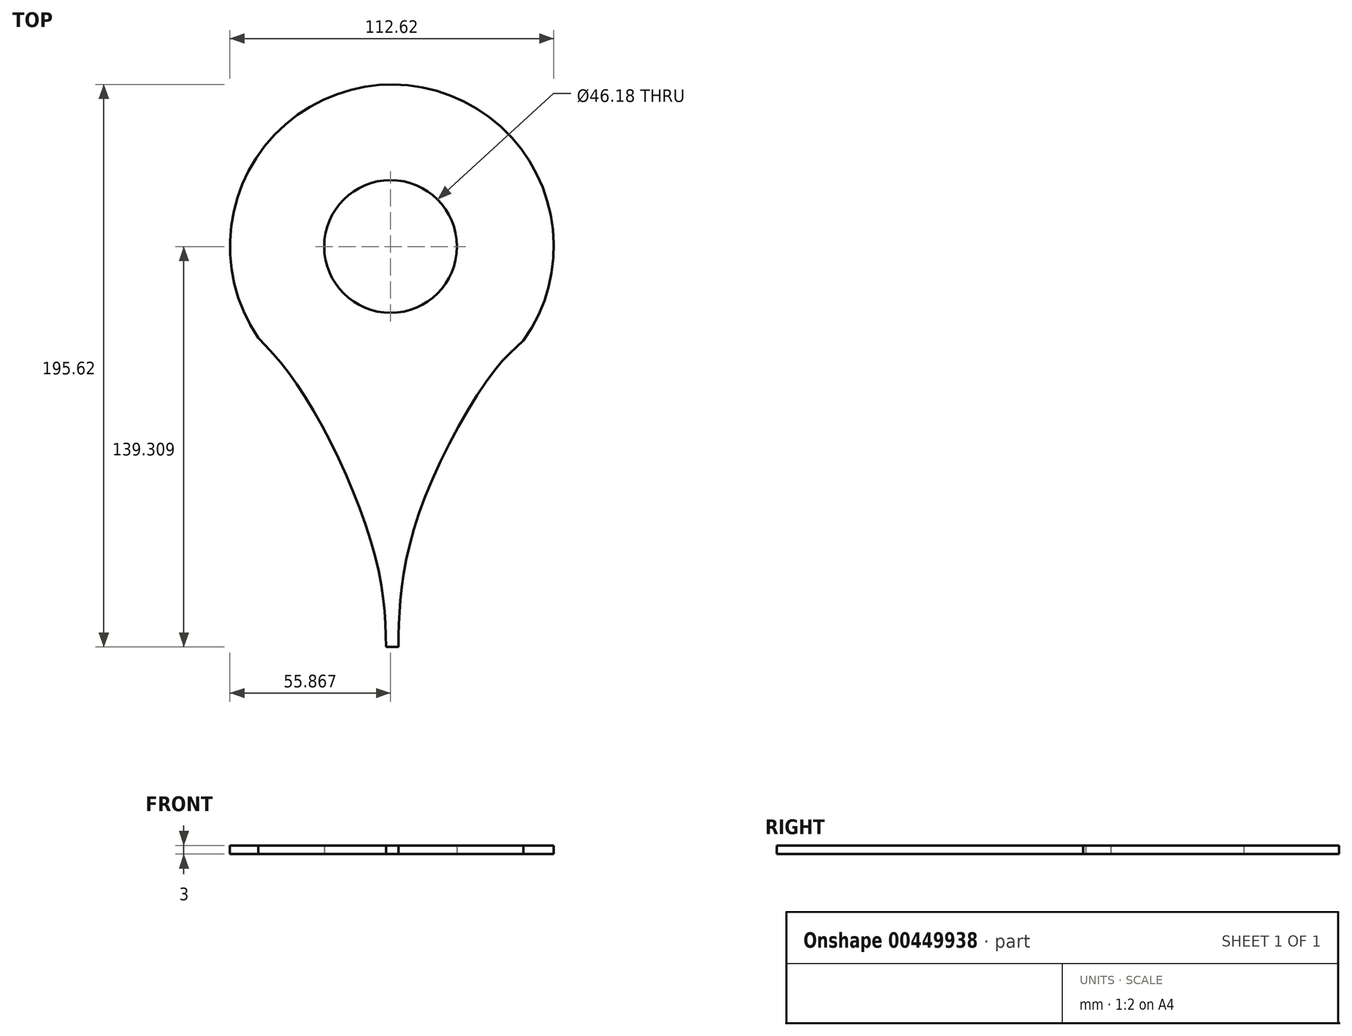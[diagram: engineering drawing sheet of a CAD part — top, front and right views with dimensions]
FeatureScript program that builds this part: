
annotation { "Feature Type Name" : "Feature", "Feature Type Description" : "" }
export const myFeature = defineFeature(function(context is Context, id is Id, definition is map)
    precondition{}
    {
        {
            var Q0;
            Q0=qCreatedBy(makeId("Top.planeOp"),FACE);
            var sketch = newSketch(context, id + "F0", { "sketchPlane" : qUnion([Q0])});
            skCircle(sketch, "E0", {"center": v(-15.91, 53.5) * mm, "radius": 23.09 * mm});
            skPoint(sketch, "E0.first.point", {"position": v(-33.82, 68.09) * mm});
            skPoint(sketch, "E0.second.point", {"position": v(6.07, 60.56) * mm});
            skPoint(sketch, "E0.third.point", {"position": v(-14.4, 30.47) * mm});
            skSolve(sketch);
        }
        {
            var Q0;
            Q0=qCreatedBy(makeId("Top.planeOp"),FACE);
            var sketch = newSketch(context, id + "F1", { "sketchPlane" : qUnion([Q0])});
            skArc(sketch, "E1", {"start": v(24.44, 13.77) * mm, "mid": v(-14.44, 109.8) * mm, "end": v(-56.8, 15.26) * mm});
            skPoint(sketch, "E1.first.point", {"position": v(-61.18, 86.39) * mm});
            skPoint(sketch, "E1.second.point", {"position": v(6.74, 105.25) * mm});
            skPoint(sketch, "E1.third.point", {"position": v(40.25, 61.65) * mm});
            skFitSpline(sketch, "E2", {"points": [v(-13.17, -85.8) * mm, v(0, -30.44) * mm, v(30.34, 20.75) * mm], "startDerivative": vector(6.32, 122.94) * mm, "endDerivative": vector(65.3, 68.34) * mm});
            skFitSpline(sketch, "E3", {"points": [v(-17.45, -85.75) * mm, v(-31.97, -29.34) * mm, v(-61.95, 21.71) * mm], "startDerivative": vector(-9.54, 126.56) * mm, "endDerivative": vector(-75.08, 88.5) * mm});
            skLineSegment(sketch, "E4", {"start": v(-17.45, -85.75) * mm, "end": v(-13.17, -85.8) * mm});
            skSolve(sketch);
        }
        {
            var Q0;
            Q0=makeQuery(id+"F0.imprint","IMPRINT",FACE,{"disambiguationData":[TD([[makeQuery(id+"F0.imprint","IMPRINT",EDGE,{"derivedFrom":sQuery(id+"F0.wireOp",EDGE,"E0")}),1.0]])]});
            var sketch = newSketch(context, id + "F2", { "sketchPlane" : qUnion([Q0])});
            skCircle(sketch, "E5.0", {"center": v(-15.91, 53.5) * mm, "radius": 23.09 * mm});
            skArc(sketch, "E6.0", {"start": v(24.44, 13.77) * mm, "mid": v(-14.44, 109.8) * mm, "end": v(-56.8, 15.26) * mm});
            skFitSpline(sketch, "E7.0", {"points": [v(-17.45, -85.75) * mm, v(-19.04, -64.74) * mm, v(-29.85, -29.46) * mm, v(-49.39, 6.9) * mm, v(-61.95, 21.71) * mm]});
            skFitSpline(sketch, "E8.0", {"points": [v(-13.17, -85.8) * mm, v(-12.12, -65.54) * mm, v(-3.25, -31.9) * mm, v(19.33, 9.23) * mm, v(30.34, 20.75) * mm]});
            skPoint(sketch, "E9.0", {"position": v(-15.31, -85.77) * mm});
            skLineSegment(sketch, "E10.0", {"start": v(-17.45, -85.75) * mm, "end": v(-13.17, -85.8) * mm});
            skSolve(sketch);
        }
        {
            var Q0;
            Q0=qSketchRegion(id+"F2",true);
            extrude(context, id + "F3", {"entities" : qUnion([Q0]), "depth" : 3 * mm});
        }
        {
            var Q0;
            Q0=qSketchRegion(id+"F0",true);
            extrude(context, id + "F4", {"entities" : qUnion([Q0]), "depth" : 3 * mm});
        }
    });
